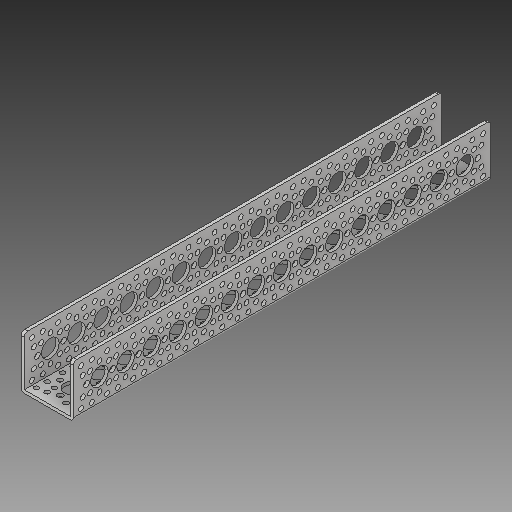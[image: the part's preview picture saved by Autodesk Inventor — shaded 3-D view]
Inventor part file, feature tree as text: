
AUTODESK INVENTOR PART (.ipt)
format: ipt  version: 2017 (Build 210142000, 142)  size: 997,376 bytes
history: native  units: in
note: dims shown in document units (in); Inventor stores cm internally (conversion verified against a paired STEP export)
features: fillet x1
ambient origin geometry x8: Origin, YZ Plane, XZ Plane, XY Plane, X Axis, Y Axis, Z Axis, Center Point
bodies: Solid1 (feature_tree)
feature tree (1):
  fillet  "Fillet1"  [1 undecoded]
note: 1 required parameter value undecoded (feature->parameter linkage not recoverable at this tier; creation-order binding heuristic only, values carry confidence <= 0.55)
